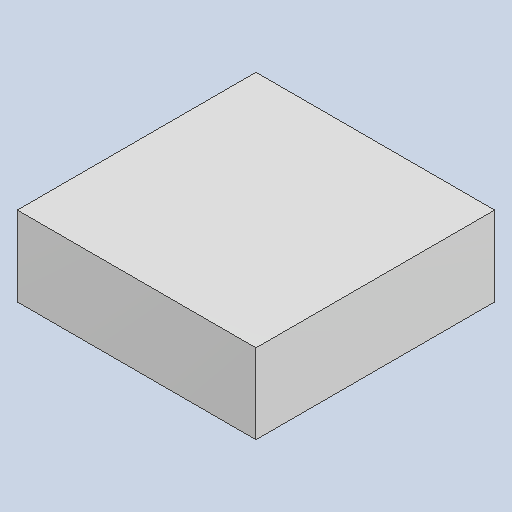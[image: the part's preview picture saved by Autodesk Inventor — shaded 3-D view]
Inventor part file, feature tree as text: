
AUTODESK INVENTOR PART (.ipt)
format: ipt  version: 2023.4 (Build 274418000, 418)  size: 79,872 bytes
history: native  units: mm
features: extrude x1
ambient origin geometry x8: Origin, YZ Plane, XZ Plane, XY Plane, X Axis, Y Axis, Z Axis, Center Point
bodies: Solid1 (feature_tree)
feature tree (1):
  extrude  "Extruded_64"  [1 undecoded]
note: 1 required parameter value undecoded (feature->parameter linkage not recoverable at this tier; creation-order binding heuristic only, values carry confidence <= 0.55)
